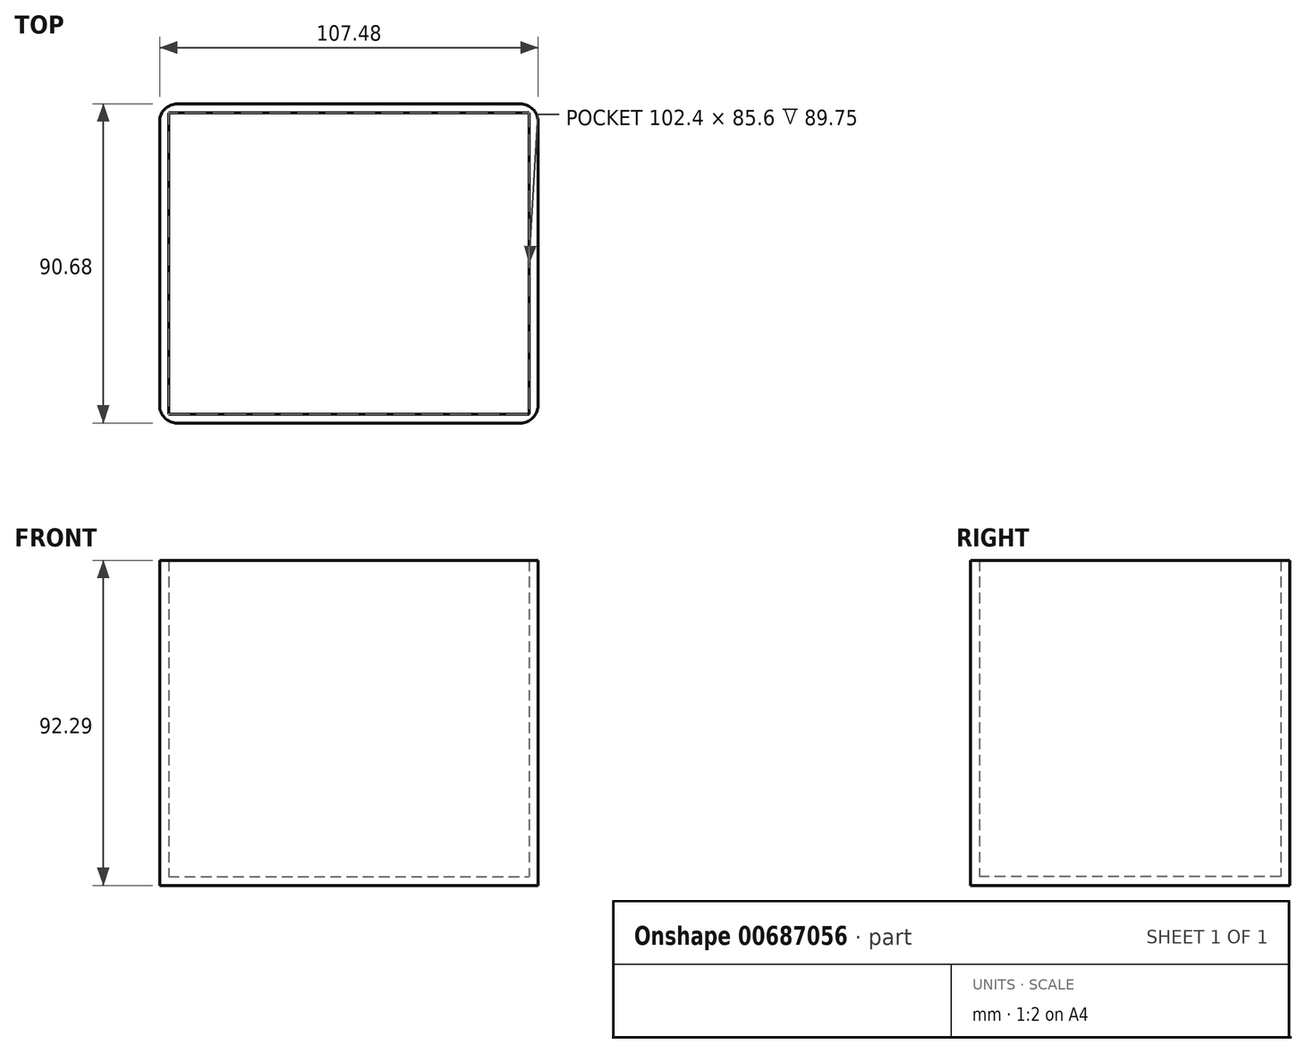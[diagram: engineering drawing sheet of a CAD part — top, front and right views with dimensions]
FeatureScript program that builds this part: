
annotation { "Feature Type Name" : "Feature", "Feature Type Description" : "" }
export const myFeature = defineFeature(function(context is Context, id is Id, definition is map)
    precondition{}
    {
        {
            var Q0;
            Q0=qCreatedBy(makeId("Top.planeOp"),FACE);
            var sketch = newSketch(context, id + "F0", { "sketchPlane" : qUnion([Q0])});
            skLineSegment(sketch, "E0.bottom", {"start": v(-50.52, 49.93) * mm, "end": v(51.88, 49.93) * mm});
            skLineSegment(sketch, "E0.top", {"start": v(-50.52, -35.67) * mm, "end": v(51.88, -35.67) * mm});
            skLineSegment(sketch, "E0.left", {"start": v(-50.52, 49.93) * mm, "end": v(-50.52, -35.67) * mm});
            skLineSegment(sketch, "E0.right", {"start": v(51.88, 49.93) * mm, "end": v(51.88, -35.67) * mm});
            skSolve(sketch);
        }
        {
            var Q0;
            Q0=makeQuery(id+"F0.imprint","IMPRINT",FACE,{"disambiguationData":[TD([[makeQuery(id+"F0.imprint","IMPRINT",EDGE,{"derivedFrom":sQuery(id+"F0.wireOp",EDGE,"E0.bottom")}),-1.0]])]});
            extrude(context, id + "F1", {"entities" : qUnion([Q0]), "depth" : 89.75 * mm, "offsetDistance" : 25.4 * mm});
        }
        {
            var Q0;
            Q0=makeQuery(id+"F1.opExtrude","CAP_FACE",FACE,{"disambiguationData":[OSD([sQuery(id+"F0.wireOp",EDGE,"E0.bottom"),sQuery(id+"F0.wireOp",EDGE,"E0.top"),sQuery(id+"F0.wireOp",EDGE,"E0.left"),sQuery(id+"F0.wireOp",EDGE,"E0.right")])],"isStart":false});
            shell(context, id + "F2", {"entities" : qUnion([Q0]), "thickness" : 2.54 * mm, "oppositeDirection" : true});
        }
        {
            var Q0;
            Q0=makeQuery(id+"F1.opExtrude","SWEPT_EDGE",EDGE,{"disambiguationData":[OSD([sQuery(id+"F0.wireOp",EDGE,"E0.top"),sQuery(id+"F0.wireOp",EDGE,"E0.right")])]});
            var Q1;
            Q1=makeQuery(id+"F1.opExtrude","SWEPT_EDGE",EDGE,{"disambiguationData":[OSD([sQuery(id+"F0.wireOp",EDGE,"E0.bottom"),sQuery(id+"F0.wireOp",EDGE,"E0.right")])]});
            var Q2;
            Q2=makeQuery(id+"F1.opExtrude","SWEPT_EDGE",EDGE,{"disambiguationData":[OSD([sQuery(id+"F0.wireOp",EDGE,"E0.bottom"),sQuery(id+"F0.wireOp",EDGE,"E0.left")])]});
            var Q3;
            Q3=makeQuery(id+"F1.opExtrude","SWEPT_EDGE",EDGE,{"disambiguationData":[OSD([sQuery(id+"F0.wireOp",EDGE,"E0.top"),sQuery(id+"F0.wireOp",EDGE,"E0.left")])]});
            fillet(context, id + "F3", {"entities" : qUnion([Q0, Q1, Q2, Q3]), "radius" : 5.08 * mm, "tangentPropagation" : true, "allowEdgeOverflow" : false});
        }
    });
